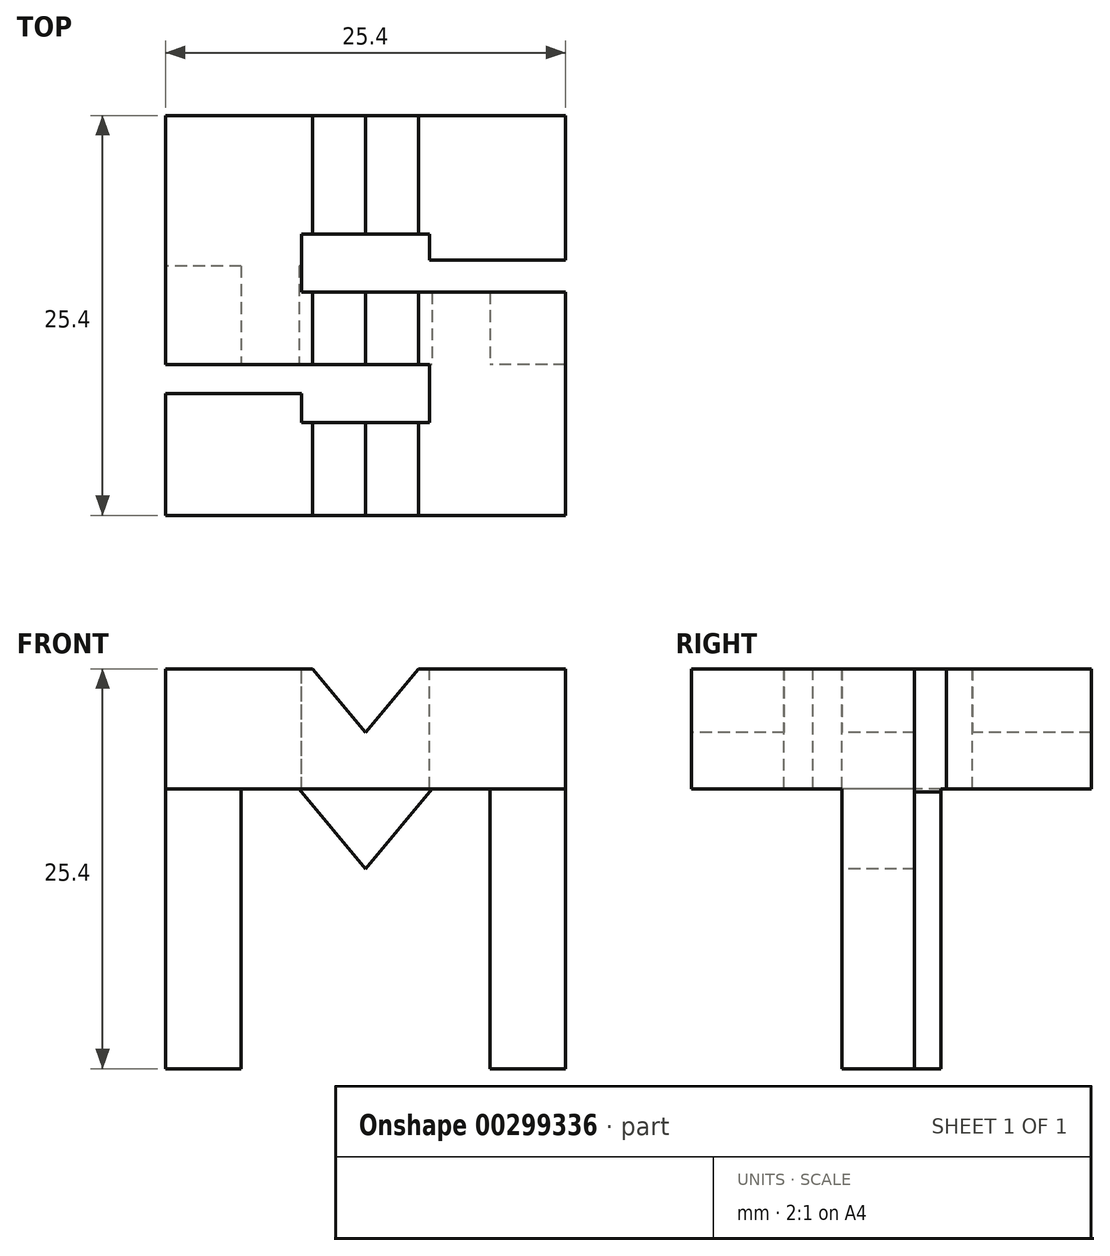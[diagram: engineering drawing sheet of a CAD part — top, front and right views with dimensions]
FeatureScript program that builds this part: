
annotation { "Feature Type Name" : "Feature", "Feature Type Description" : "" }
export const myFeature = defineFeature(function(context is Context, id is Id, definition is map)
    precondition{}
    {
        {
            var Q0;
            Q0=qCreatedBy(makeId("Top.planeOp"),FACE);
            var sketch = newSketch(context, id + "F0", { "sketchPlane" : qUnion([Q0])});
            skLineSegment(sketch, "E0.bottom", {"start": v(12.7, 12.7) * mm, "end": v(-12.7, 12.7) * mm});
            skLineSegment(sketch, "E0.top", {"start": v(12.7, -12.7) * mm, "end": v(-12.7, -12.7) * mm});
            skLineSegment(sketch, "E0.left", {"start": v(12.7, 12.7) * mm, "end": v(12.7, -12.7) * mm});
            skLineSegment(sketch, "E0.right", {"start": v(-12.7, 12.7) * mm, "end": v(-12.7, -12.7) * mm});
            skPoint(sketch, "E0.middle", {"position": v(0, 0) * mm});
            skSolve(sketch);
        }
        {
            var Q0;
            Q0=makeQuery(id+"F0.imprint","IMPRINT",FACE,{"disambiguationData":[TD([[makeQuery(id+"F0.imprint","IMPRINT",EDGE,{"derivedFrom":sQuery(id+"F0.wireOp",EDGE,"E0.bottom")}),1.0]])]});
            extrude(context, id + "F1", {"entities" : qUnion([Q0]), "depth" : 25.4 * mm});
        }
        {
            var Q0;
            Q0=makeQuery(id+"F1.opExtrude","CAP_FACE",FACE,{"disambiguationData":[OSD([sQuery(id+"F0.wireOp",EDGE,"E0.bottom"),sQuery(id+"F0.wireOp",EDGE,"E0.top"),sQuery(id+"F0.wireOp",EDGE,"E0.left"),sQuery(id+"F0.wireOp",EDGE,"E0.right")])],"isStart":false});
            var sketch = newSketch(context, id + "F2", { "sketchPlane" : qUnion([Q0])});
            skLineSegment(sketch, "E1", {"start": v(-12.7, 0) * mm, "end": v(12.7, 0) * mm});
            skLineSegment(sketch, "E2", {"start": v(0, 12.7) * mm, "end": v(0, -12.7) * mm});
            skLineSegment(sketch, "E3.bottom", {"start": v(4.05, 5.16) * mm, "end": v(-4.05, 5.16) * mm});
            skLineSegment(sketch, "E3.top", {"start": v(4.05, 1.47) * mm, "end": v(-4.05, 1.47) * mm});
            skLineSegment(sketch, "E3.left", {"start": v(4.05, 5.16) * mm, "end": v(4.05, 1.47) * mm});
            skLineSegment(sketch, "E3.right", {"start": v(-4.05, 5.16) * mm, "end": v(-4.05, 1.47) * mm});
            skPoint(sketch, "E3.middle", {"position": v(0, 3.31) * mm});
            skLineSegment(sketch, "E4.bottom", {"start": v(4.05, 1.47) * mm, "end": v(12.7, 1.47) * mm});
            skLineSegment(sketch, "E4.top", {"start": v(4.05, 3.5) * mm, "end": v(12.7, 3.5) * mm});
            skLineSegment(sketch, "E4.left", {"start": v(4.05, 1.47) * mm, "end": v(4.05, 3.5) * mm});
            skLineSegment(sketch, "E4.right", {"start": v(12.7, 1.47) * mm, "end": v(12.7, 3.5) * mm});
            skLineSegment(sketch, "E5.bottom", {"start": v(4.05, -3.13) * mm, "end": v(-4.05, -3.13) * mm});
            skLineSegment(sketch, "E5.top", {"start": v(4.05, -6.81) * mm, "end": v(-4.05, -6.81) * mm});
            skLineSegment(sketch, "E5.left", {"start": v(4.05, -3.13) * mm, "end": v(4.05, -6.81) * mm});
            skLineSegment(sketch, "E5.right", {"start": v(-4.05, -3.13) * mm, "end": v(-4.05, -6.81) * mm});
            skPoint(sketch, "E5.middle", {"position": v(0, -4.97) * mm});
            skLineSegment(sketch, "E6.bottom", {"start": v(-4.05, -3.13) * mm, "end": v(-12.7, -3.13) * mm});
            skLineSegment(sketch, "E6.top", {"start": v(-4.05, -4.97) * mm, "end": v(-12.7, -4.97) * mm});
            skLineSegment(sketch, "E6.left", {"start": v(-4.05, -3.13) * mm, "end": v(-4.05, -4.97) * mm});
            skLineSegment(sketch, "E6.right", {"start": v(-12.7, -3.13) * mm, "end": v(-12.7, -4.97) * mm});
            skSolve(sketch);
        }
        {
            var Q0;
            {var subQ0=sQuery(id+"F2.wireOp",EDGE,"E3.left");Q0=makeQuery(id+"F2.imprint","IMPRINT",FACE,{"disambiguationData":[TD([[makeQuery(id+"F2.imprint","IMPRINT",EDGE,{"derivedFrom":subQ0}),-1.0]])]});}
            var Q1;
            {var subQ5=sQuery(id+"F2.wireOp",EDGE,"E3.right");Q1=makeQuery(id+"F2.imprint","IMPRINT",FACE,{"disambiguationData":[TD([[makeQuery(id+"F2.imprint","IMPRINT",EDGE,{"derivedFrom":subQ5}),1.0]])]});}
            var Q2;
            Q2=makeQuery(id+"F2.imprint","IMPRINT",FACE,{"disambiguationData":[TD([[makeQuery(id+"F2.imprint","IMPRINT",EDGE,{"derivedFrom":sQuery(id+"F2.wireOp",EDGE,"E4.bottom")}),1.0]])]});
            var Q3;
            Q3=makeQuery(id+"F2.imprint","IMPRINT",FACE,{"disambiguationData":[TD([[makeQuery(id+"F2.imprint","IMPRINT",EDGE,{"derivedFrom":sQuery(id+"F2.wireOp",EDGE,"E6.bottom")}),1.0]])]});
            var Q4;
            {var subQ0=sQuery(id+"F2.wireOp",EDGE,"E5.right");Q4=makeQuery(id+"F2.imprint","IMPRINT",FACE,{"disambiguationData":[TD([[makeQuery(id+"F2.imprint","IMPRINT",EDGE,{"derivedFrom":subQ0}),1.0]])]});}
            var Q5;
            {var subQ5=sQuery(id+"F2.wireOp",EDGE,"E5.left");Q5=makeQuery(id+"F2.imprint","IMPRINT",FACE,{"disambiguationData":[TD([[makeQuery(id+"F2.imprint","IMPRINT",EDGE,{"derivedFrom":subQ5}),-1.0]])]});}
            extrude(context, id + "F3", {"entities" : qUnion([Q0, Q1, Q2, Q3, Q4, Q5]), "operationType" : NewBodyOperationType.REMOVE, "oppositeDirection" : true, "depth" : 25.4 * mm});
        }
        {
            var Q0;
            Q0=makeQuery(id+"F1.opExtrude","SWEPT_FACE",FACE,{"disambiguationData":[OSD([sQuery(id+"F0.wireOp",EDGE,"E0.top")])]});
            var sketch = newSketch(context, id + "F4", { "sketchPlane" : qUnion([Q0])});
            skLineSegment(sketch, "E7", {"start": v(0, 0) * mm, "end": v(0, 25.4) * mm});
            skLineSegment(sketch, "E8", {"start": v(-12.7, 12.7) * mm, "end": v(12.7, 12.7) * mm});
            skLineSegment(sketch, "E9.bottom", {"start": v(-4.22, 0) * mm, "end": v(-7.9, 0) * mm});
            skLineSegment(sketch, "E9.top", {"start": v(-4.22, 17.78) * mm, "end": v(-7.9, 17.78) * mm});
            skLineSegment(sketch, "E9.left", {"start": v(-4.22, 0) * mm, "end": v(-4.22, 17.78) * mm});
            skLineSegment(sketch, "E9.right", {"start": v(-7.9, 0) * mm, "end": v(-7.9, 17.78) * mm});
            skLineSegment(sketch, "E10.bottom", {"start": v(7.9, 0) * mm, "end": v(4.22, 0) * mm});
            skLineSegment(sketch, "E10.top", {"start": v(7.9, 17.78) * mm, "end": v(4.22, 17.78) * mm});
            skLineSegment(sketch, "E10.left", {"start": v(7.9, 0) * mm, "end": v(7.9, 17.78) * mm});
            skLineSegment(sketch, "E10.right", {"start": v(4.22, 0) * mm, "end": v(4.22, 17.78) * mm});
            skLineSegment(sketch, "E11", {"start": v(0, 21.35) * mm, "end": v(3.36, 25.4) * mm});
            skLineSegment(sketch, "E12", {"start": v(0, 21.35) * mm, "end": v(-3.36, 25.4) * mm});
            skLineSegment(sketch, "E13", {"start": v(-4.22, 17.78) * mm, "end": v(0, 12.7) * mm});
            skLineSegment(sketch, "E14", {"start": v(0, 12.7) * mm, "end": v(4.22, 17.78) * mm});
            skSolve(sketch);
        }
        {
            var Q0;
            {var subQ0=sQuery(id+"F0.wireOp",EDGE,"E0.bottom");var subQ1=sQuery(id+"F0.wireOp",EDGE,"E0.right");Q0=makeQuery(id+"F3.boolean.opBoolean","SPLIT",FACE,{"disambiguationData":[TD([makeQuery(id+"F1.opExtrude","SWEPT_FACE",FACE,{"disambiguationData":[OSD([subQ0])]})])],"derivedFrom":makeQuery(id+"F1.opExtrude","SWEPT_FACE",FACE,{"disambiguationData":[OSD([subQ1])]})});}
            var sketch = newSketch(context, id + "F5", { "sketchPlane" : qUnion([Q0])});
            skLineSegment(sketch, "E15.bottom", {"start": v(-12.7, 17.78) * mm, "end": v(-3.13, 17.78) * mm});
            skLineSegment(sketch, "E15.top", {"start": v(-12.7, 0) * mm, "end": v(-3.13, 0) * mm});
            skLineSegment(sketch, "E15.left", {"start": v(-12.7, 17.78) * mm, "end": v(-12.7, 0) * mm});
            skLineSegment(sketch, "E15.right", {"start": v(-3.13, 17.78) * mm, "end": v(-3.13, 0) * mm});
            skLineSegment(sketch, "E16.bottom", {"start": v(3.13, 17.78) * mm, "end": v(12.7, 17.78) * mm});
            skLineSegment(sketch, "E16.top", {"start": v(3.13, 0) * mm, "end": v(12.7, 0) * mm});
            skLineSegment(sketch, "E16.left", {"start": v(3.13, 17.78) * mm, "end": v(3.13, 0) * mm});
            skLineSegment(sketch, "E16.right", {"start": v(12.7, 17.78) * mm, "end": v(12.7, 0) * mm});
            skSolve(sketch);
        }
        {
            var Q0;
            Q0=makeQuery(id+"F5.imprint","IMPRINT",FACE,{"disambiguationData":[TD([[makeQuery(id+"F5.imprint","IMPRINT",EDGE,{"derivedFrom":sQuery(id+"F5.wireOp",EDGE,"E15.bottom")}),-1.0]])]});
            var Q1;
            Q1=makeQuery(id+"F5.imprint","IMPRINT",FACE,{"disambiguationData":[TD([[makeQuery(id+"F5.imprint","IMPRINT",EDGE,{"derivedFrom":sQuery(id+"F5.wireOp",EDGE,"E16.bottom")}),-1.0]])]});
            extrude(context, id + "F6", {"entities" : qUnion([Q0, Q1]), "operationType" : NewBodyOperationType.REMOVE, "oppositeDirection" : true, "depth" : 25.4 * mm});
        }
        {
            var Q0;
            Q0 = qSketchRegion(id + "F4", true);
            var Q1;
            {var subQ3=sQuery(id+"F4.wireOp",EDGE,"E8");var subQ5=sQuery(id+"F4.wireOp",EDGE,"E10.right");var subQ6=makeQuery(id+"F4.imprint","INTERSECT",VERTEX,{"derivedFrom":[subQ3,subQ5]});Q1=makeQuery(id+"F4.imprint","IMPRINT",FACE,{"disambiguationData":[TD([[makeQuery(id+"F4.imprint","IMPRINT",EDGE,{"disambiguationData":[TD([[subQ6,1.0]])],"derivedFrom":subQ5}),1.0]])]});}
            var Q2;
            {var subQ3=sQuery(id+"F4.wireOp",EDGE,"E8");var subQ5=sQuery(id+"F4.wireOp",EDGE,"E9.left");var subQ6=makeQuery(id+"F4.imprint","INTERSECT",VERTEX,{"derivedFrom":[subQ3,subQ5]});Q2=makeQuery(id+"F4.imprint","IMPRINT",FACE,{"disambiguationData":[TD([[makeQuery(id+"F4.imprint","IMPRINT",EDGE,{"disambiguationData":[TD([[subQ6,1.0]])],"derivedFrom":subQ5}),-1.0]])]});}
            var Q3;
            {var subQ3=sQuery(id+"F4.wireOp",EDGE,"E11");Q3=makeQuery(id+"F4.imprint","IMPRINT",FACE,{"disambiguationData":[TD([[makeQuery(id+"F4.imprint","IMPRINT",EDGE,{"derivedFrom":subQ3}),1.0]])]});}
            var Q4;
            {var subQ3=sQuery(id+"F4.wireOp",EDGE,"E12");Q4=makeQuery(id+"F4.imprint","IMPRINT",FACE,{"disambiguationData":[TD([[makeQuery(id+"F4.imprint","IMPRINT",EDGE,{"derivedFrom":subQ3}),-1.0]])]});}
            extrude(context, id + "F7", {"entities" : qUnion([Q0, Q1, Q2, Q3, Q4]), "operationType" : NewBodyOperationType.REMOVE, "oppositeDirection" : true, "depth" : 25.4 * mm});
        }
    });
